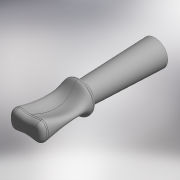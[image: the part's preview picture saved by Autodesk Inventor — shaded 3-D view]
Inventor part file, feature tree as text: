
AUTODESK INVENTOR PART (.ipt)
format: ipt  version: 2018 (Build 220112000, 112)  size: 339,456 bytes
history: native  units: in
note: dims shown in document units (in); Inventor stores cm internally (conversion verified against a paired STEP export)
features: other x5, extrude x3, loft x3, fillet x2, plane x1, sheet_metal_op x1
ambient origin geometry x8: Origin, YZ Plane, XZ Plane, XY Plane, X Axis, Y Axis, Z Axis, Center Point
bodies: Solid1 (feature_tree)
feature tree (15):
  extrude  "Plug"  [1 undecoded]
  extrude  "Extrusion2"  Depth=0.3937in
  plane  "Work Plane1"
  extrude  "Cap"  TaperAngle=0.0deg  [1 undecoded]
  loft  "Handle Loft"
  sheet_metal_op  "Notch"
  fillet  "Fillet1"  Radius=0.0787in
  fillet  "Fillet4"  Radius=0.3937in
  other  "Plug Size"
  other  "Handle End Sketch"
  loft  "Loft Rails"
  loft  "Loft Start"
  other  "Notch Sketch"
  other  "Edges6"
  other  "Edges8"
note: 2 required parameter values undecoded (feature->parameter linkage not recoverable at this tier; creation-order binding heuristic only, values carry confidence <= 0.55)
